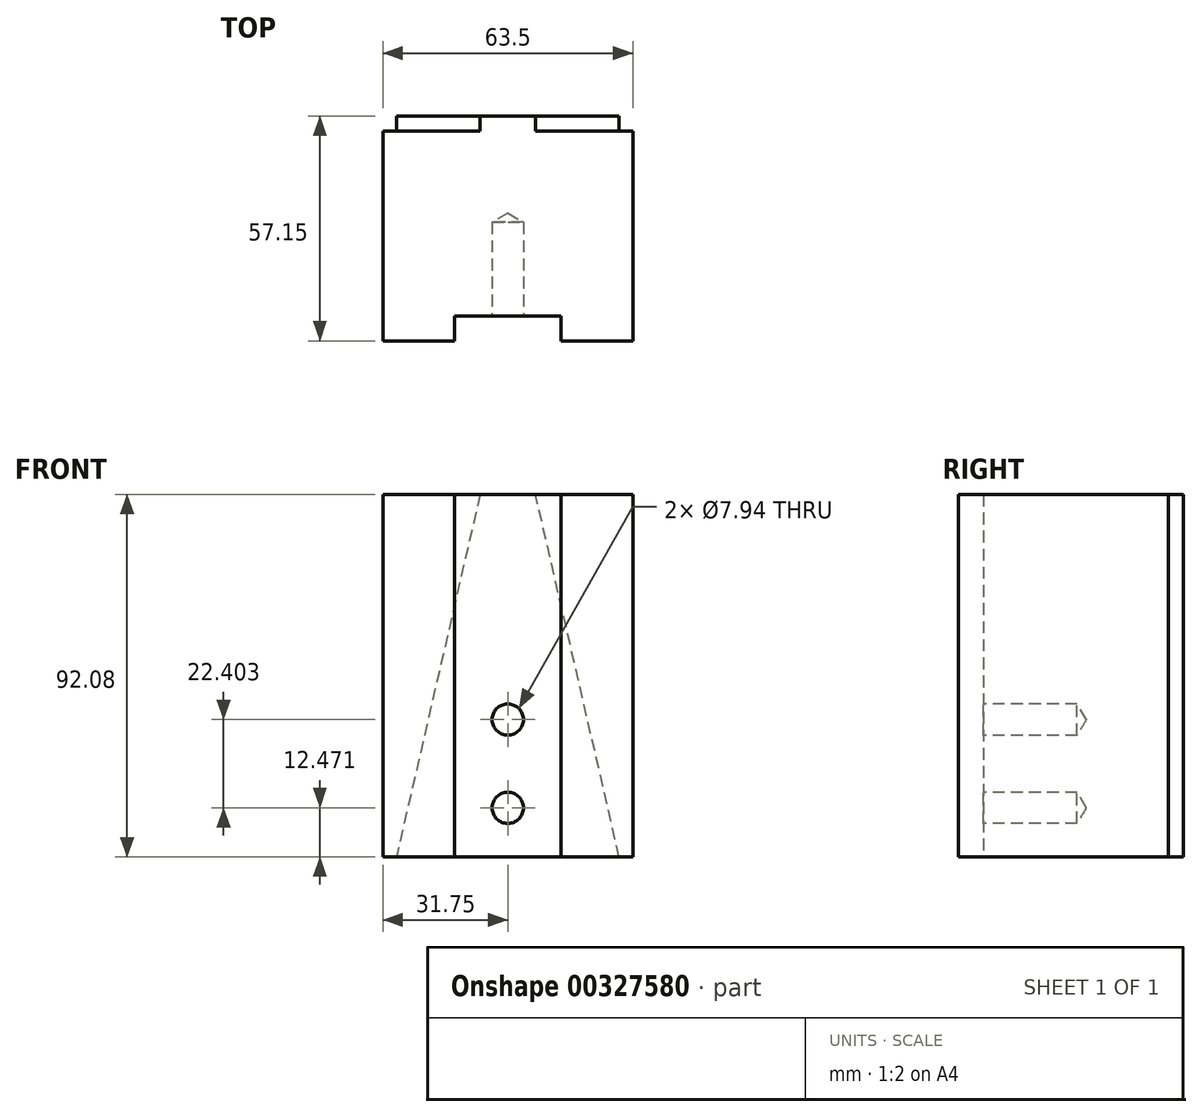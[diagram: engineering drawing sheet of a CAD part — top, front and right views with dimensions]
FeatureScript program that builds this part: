
annotation { "Feature Type Name" : "Feature", "Feature Type Description" : "" }
export const myFeature = defineFeature(function(context is Context, id is Id, definition is map)
    precondition{}
    {
        {
            var Q0;
            Q0=qCreatedBy(makeId("Top.planeOp"),FACE);
            var sketch = newSketch(context, id + "F0", { "sketchPlane" : qUnion([Q0])});
            skLineSegment(sketch, "E0", {"start": v(-31.75, 0) * mm, "end": v(-31.75, 57.15) * mm});
            skLineSegment(sketch, "E1", {"start": v(-31.75, 57.15) * mm, "end": v(31.75, 57.15) * mm});
            skLineSegment(sketch, "E2", {"start": v(31.75, 57.15) * mm, "end": v(31.75, 0) * mm});
            skLineSegment(sketch, "E3", {"start": v(31.75, 0) * mm, "end": v(13.53, 0) * mm});
            skLineSegment(sketch, "E4", {"start": v(13.53, 0) * mm, "end": v(13.53, 6.35) * mm});
            skLineSegment(sketch, "E5", {"start": v(13.53, 6.35) * mm, "end": v(-13.53, 6.35) * mm});
            skLineSegment(sketch, "E6", {"start": v(-13.53, 6.35) * mm, "end": v(-13.53, 0) * mm});
            skLineSegment(sketch, "E7", {"start": v(-13.53, 0) * mm, "end": v(-31.75, 0) * mm});
            skSolve(sketch);
        }
        {
            var Q0;
            Q0=makeQuery(id+"F0.imprint","IMPRINT",FACE,{"disambiguationData":[TD([[makeQuery(id+"F0.imprint","IMPRINT",EDGE,{"derivedFrom":sQuery(id+"F0.wireOp",EDGE,"E0")}),-1.0]])]});
            extrude(context, id + "F1", {"entities" : qUnion([Q0]), "depth" : 92.07 * mm});
        }
        {
            var Q0;
            Q0=makeQuery(id+"F1.opExtrude","SWEPT_FACE",FACE,{"disambiguationData":[OSD([sQuery(id+"F0.wireOp",EDGE,"E5")])]});
            var sketch = newSketch(context, id + "F2", { "sketchPlane" : qUnion([Q0])});
            skCircle(sketch, "E8", {"center": v(0, 12.47) * mm, "radius": 3.97 * mm});
            skCircle(sketch, "E9", {"center": v(0, 34.87) * mm, "radius": 3.97 * mm});
            skSolve(sketch);
        }
        {
            var Q0;
            Q0=sQuery(id+"F2.wireOp",VERTEX,"E9.center");
            var Q1;
            Q1=sQuery(id+"F2.wireOp",VERTEX,"E8.center");
            var Q2;
            Q2=makeQuery(id+"F1.opExtrude","SWEPT_BODY",BODY,{"disambiguationData":[OSD([sQuery(id+"F0.wireOp",EDGE,"E0"),sQuery(id+"F0.wireOp",EDGE,"E1"),sQuery(id+"F0.wireOp",EDGE,"E2"),sQuery(id+"F0.wireOp",EDGE,"E3"),sQuery(id+"F0.wireOp",EDGE,"E4"),sQuery(id+"F0.wireOp",EDGE,"E5"),sQuery(id+"F0.wireOp",EDGE,"E6"),sQuery(id+"F0.wireOp",EDGE,"E7")])]});
            hole(context, id + "F3", {"style" : HoleStyle.SIMPLE, "endStyle" : HoleEndStyle.BLIND, "standardTappedOrClearance" : lookupTablePath({ "standard" : "ANSI", "engagement" : "75%", "pitch" : "16 tpi", "size" : "3/8", "type" : "Tapped" }), "standardBlindInLast" : lookupTablePath({ "standard" : "ANSI", "engagement" : "75%", "pitch" : "16 tpi", "size" : "3/8", "type" : "Tapped" }), "holeDiameter" : 7.94 * mm, "showTappedDepth" : true, "holeDepth" : 23.8 * mm, "tappedDepth" : 19.04 * mm, "tapClearance" : 3, "locations" : qUnion([Q0, Q1]), "scope" : qUnion([Q2]), "majorDiameter" : 9.53 * mm});
        }
        {
            var Q0;
            Q0=makeQuery(id+"F1.opExtrude","SWEPT_FACE",FACE,{"disambiguationData":[OSD([sQuery(id+"F0.wireOp",EDGE,"E1")])]});
            var sketch = newSketch(context, id + "F4", { "sketchPlane" : qUnion([Q0])});
            skLineSegment(sketch, "E10", {"start": v(-28.3, 0) * mm, "end": v(-7.05, 92.08) * mm});
            skLineSegment(sketch, "E11", {"start": v(-7.05, 92.07) * mm, "end": v(7.05, 92.07) * mm});
            skLineSegment(sketch, "E12", {"start": v(7.05, 92.08) * mm, "end": v(28.3, 0) * mm});
            skLineSegment(sketch, "E13", {"start": v(28.3, 0) * mm, "end": v(-28.3, 0) * mm});
            skSolve(sketch);
        }
        {
            var Q0;
            {var subQ0=sQuery(id+"F4.wireOp",EDGE,"E10");Q0=makeQuery(id+"F4.imprint","IMPRINT",FACE,{"disambiguationData":[TD([[makeQuery(id+"F4.imprint","IMPRINT",EDGE,{"derivedFrom":subQ0}),1.0]])]});}
            var Q1;
            {var subQ0=sQuery(id+"F4.wireOp",EDGE,"E12");Q1=makeQuery(id+"F4.imprint","IMPRINT",FACE,{"disambiguationData":[TD([[makeQuery(id+"F4.imprint","IMPRINT",EDGE,{"derivedFrom":subQ0}),1.0]])]});}
            extrude(context, id + "F5", {"entities" : qUnion([Q0, Q1]), "operationType" : NewBodyOperationType.REMOVE, "oppositeDirection" : true, "depth" : 3.8 * mm});
        }
    });
